# Revit family: Toilet - Floor Mounted
name_source: partatom
category: Plumbing Fixtures
revit_build: Autodesk Revit 2013 (Build: 20121003_2115(x64)
units: mm (PartAtom-declared; Revit-internal decimal feet)

## types (2) — shared parameters
ADA Compliant = No
CW Connection = Yes
Cold Water Connection Diameter = 0' - 0 3/8"
Cold Water Connection Radius = 0' - 0 3/16"
Default Elevation = 0' - 0"
Description = San Raphael™ Comfort Height™ elongated Power Lite(R) toilet and C3® toilet seat with bidet functionality
Flushing System = Power Lite®
Gallons Per Flush = 1.4
HW Connection = No
Liters Per Flush = 5.3
Manufacturer = Kohler
Material = Vitreous China
Model = K-3607
Overall Height = 1' - 9 1/2"
Overall Length = 2' - 6"
Overall Width = 1' - 7 1/2"
Rough-in = 1' - 0"
Seat = K-4744
Type Comments = FLOOR-MOUNT TOILET:
URL = http://www.us.kohler.com
Vent Connection = No
Waste Connection = Yes
Waste Connection Diameter = 0' - 3"
Waste Connection Radius = 0' - 1 1/2"

## type names (no varying parameters)
- Floor Mounted Toilet - Kohler 3RD FLR
- Floor Mounted Toilet - Kohler

## geometry (parser evidence)
native form markers: Blend x4, Sweep x4
no freeform markers — native parametric forms only
